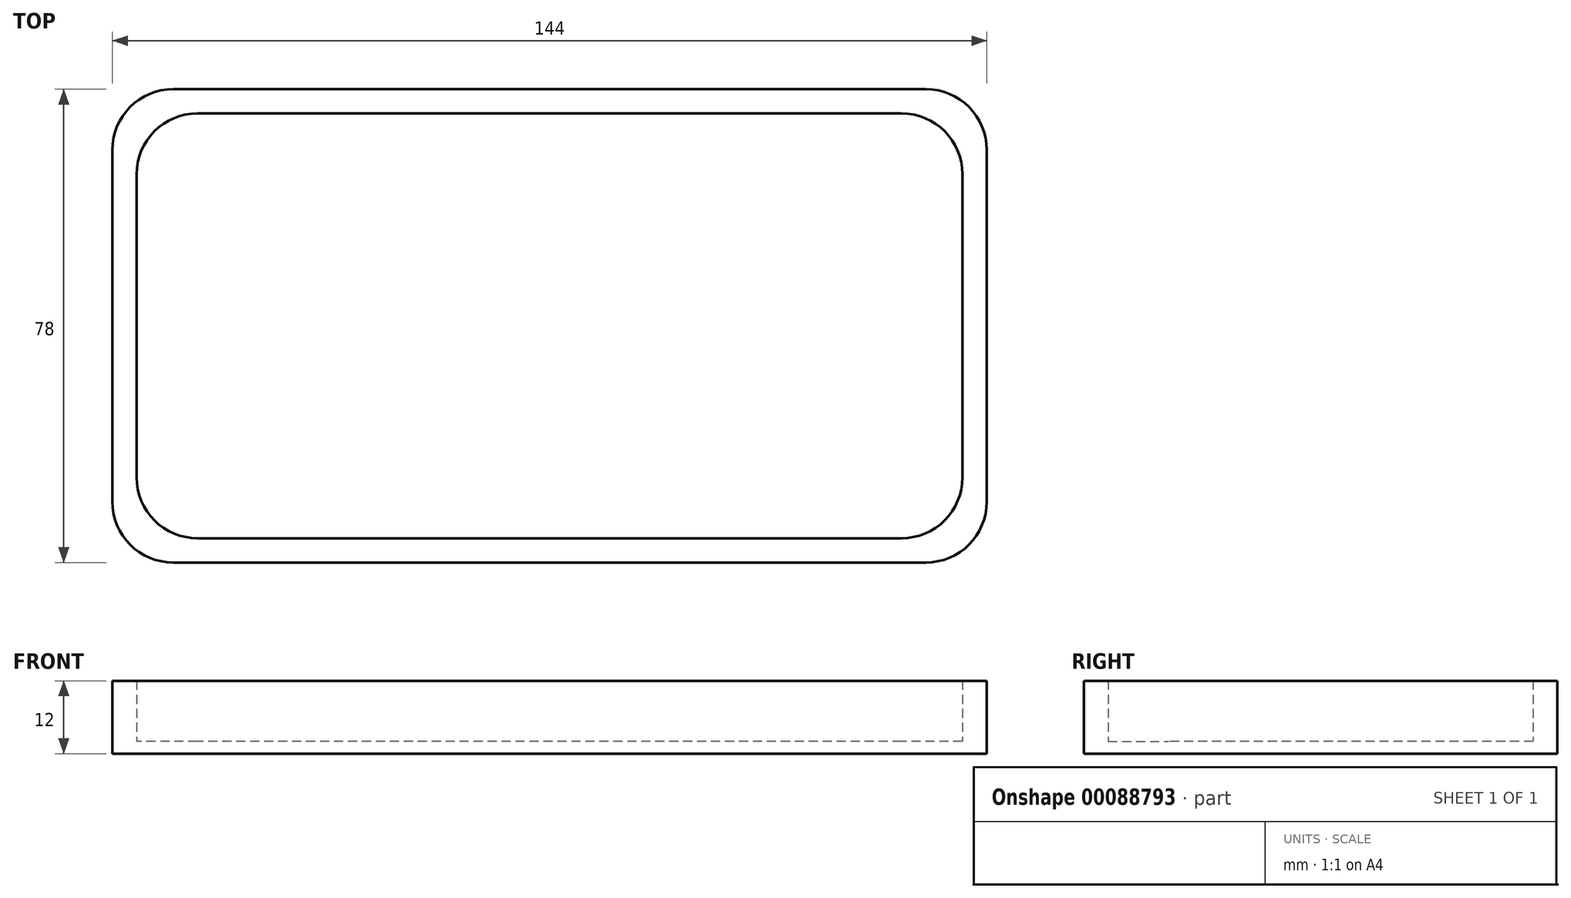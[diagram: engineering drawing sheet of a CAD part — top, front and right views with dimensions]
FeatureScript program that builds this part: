
annotation { "Feature Type Name" : "Feature", "Feature Type Description" : "" }
export const myFeature = defineFeature(function(context is Context, id is Id, definition is map)
    precondition{}
    {
        {
            var Q0;
            Q0=qCreatedBy(makeId("Top.planeOp"),FACE);
            var sketch = newSketch(context, id + "F0", { "sketchPlane" : qUnion([Q0])});
            skLineSegment(sketch, "E0.bottom", {"start": v(12.6, 34.6) * mm, "end": v(-103.4, 34.6) * mm});
            skLineSegment(sketch, "E0.top", {"start": v(12.6, -35.4) * mm, "end": v(-103.4, -35.4) * mm});
            skLineSegment(sketch, "E0.left", {"start": v(22.6, 24.6) * mm, "end": v(22.6, -25.4) * mm});
            skLineSegment(sketch, "E0.right", {"start": v(-113.4, 24.6) * mm, "end": v(-113.4, -25.4) * mm});
            skLineSegment(sketch, "E1.0", {"start": v(16.6, 38.6) * mm, "end": v(-107.4, 38.6) * mm});
            skLineSegment(sketch, "E1.1", {"start": v(26.6, 28.6) * mm, "end": v(26.6, -29.4) * mm});
            skLineSegment(sketch, "E1.2", {"start": v(16.6, -39.4) * mm, "end": v(-107.4, -39.4) * mm});
            skLineSegment(sketch, "E1.3", {"start": v(-117.4, 28.6) * mm, "end": v(-117.4, -29.4) * mm});
            skPoint(sketch, "E2.visualSharp", {"position": v(22.6, 34.6) * mm});
            skArc(sketch, "E2.filletArc", {"start": v(22.6, 24.6) * mm, "mid": v(19.68, 31.67) * mm, "end": v(12.6, 34.6) * mm});
            skPoint(sketch, "E3.visualSharp", {"position": v(-113.4, 34.6) * mm});
            skArc(sketch, "E3.filletArc", {"start": v(-103.4, 34.6) * mm, "mid": v(-110.46, 31.67) * mm, "end": v(-113.4, 24.6) * mm});
            skPoint(sketch, "E4.visualSharp", {"position": v(-113.4, -35.4) * mm});
            skArc(sketch, "E4.filletArc", {"start": v(-113.4, -25.4) * mm, "mid": v(-110.46, -32.47) * mm, "end": v(-103.4, -35.4) * mm});
            skPoint(sketch, "E5.visualSharp", {"position": v(22.6, -35.4) * mm});
            skArc(sketch, "E5.filletArc", {"start": v(12.6, -35.4) * mm, "mid": v(19.68, -32.47) * mm, "end": v(22.6, -25.4) * mm});
            skPoint(sketch, "E6.visualSharp", {"position": v(26.6, -39.4) * mm});
            skArc(sketch, "E6.filletArc", {"start": v(16.6, -39.4) * mm, "mid": v(23.68, -36.47) * mm, "end": v(26.6, -29.4) * mm});
            skPoint(sketch, "E7.visualSharp", {"position": v(26.6, 38.6) * mm});
            skArc(sketch, "E7.filletArc", {"start": v(26.6, 28.6) * mm, "mid": v(23.68, 35.67) * mm, "end": v(16.6, 38.6) * mm});
            skPoint(sketch, "E8.visualSharp", {"position": v(-117.4, 38.6) * mm});
            skArc(sketch, "E8.filletArc", {"start": v(-107.4, 38.6) * mm, "mid": v(-114.46, 35.67) * mm, "end": v(-117.4, 28.6) * mm});
            skPoint(sketch, "E9.visualSharp", {"position": v(-117.4, -39.4) * mm});
            skArc(sketch, "E9.filletArc", {"start": v(-117.4, -29.4) * mm, "mid": v(-114.46, -36.47) * mm, "end": v(-107.4, -39.4) * mm});
            skSolve(sketch);
        }
        {
            var Q0;
            Q0=makeQuery(id+"F0.imprint","IMPRINT",FACE,{"disambiguationData":[TD([[makeQuery(id+"F0.imprint","IMPRINT",EDGE,{"derivedFrom":sQuery(id+"F0.wireOp",EDGE,"E0.bottom")}),1.0]])]});
            extrude(context, id + "F1", {"entities" : qUnion([Q0]), "depth" : 2 * mm});
        }
        {
            var Q0;
            Q0=makeQuery(id+"F0.imprint","IMPRINT",FACE,{"disambiguationData":[TD([[makeQuery(id+"F0.imprint","IMPRINT",EDGE,{"derivedFrom":sQuery(id+"F0.wireOp",EDGE,"E0.bottom")}),-1.0]])]});
            extrude(context, id + "F2", {"entities" : qUnion([Q0]), "operationType" : NewBodyOperationType.ADD, "depth" : 12 * mm});
        }
    });
